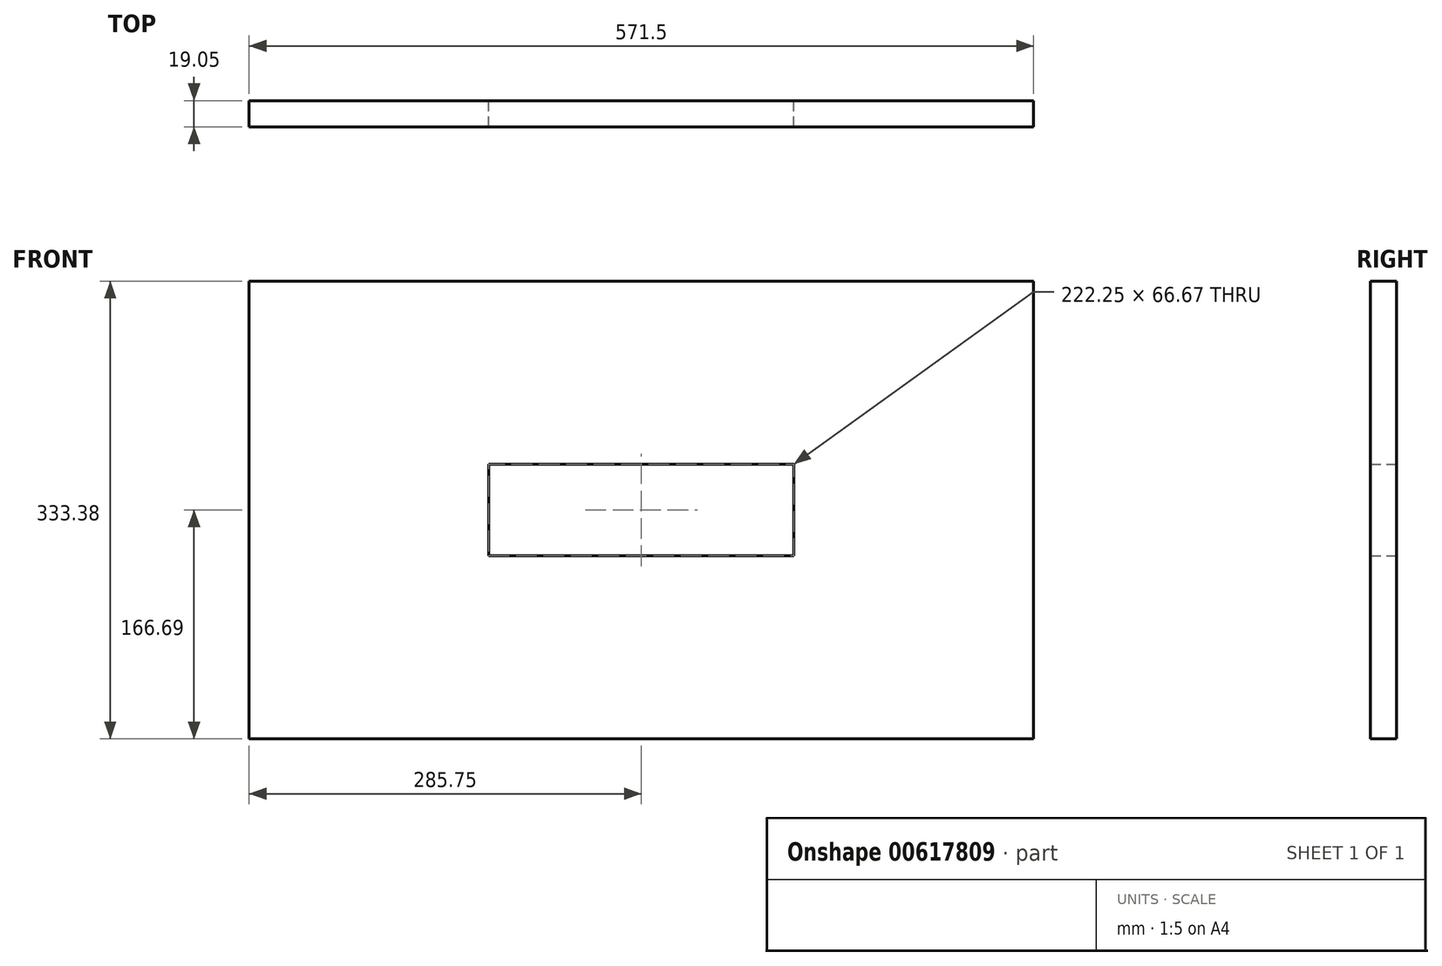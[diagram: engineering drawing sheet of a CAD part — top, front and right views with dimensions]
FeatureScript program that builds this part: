
annotation { "Feature Type Name" : "Feature", "Feature Type Description" : "" }
export const myFeature = defineFeature(function(context is Context, id is Id, definition is map)
    precondition{}
    {
        {
            var Q0;
            Q0=qCreatedBy(makeId("Front.planeOp"),FACE);
            var sketch = newSketch(context, id + "F0", { "sketchPlane" : qUnion([Q0])});
            skLineSegment(sketch, "E0.bottom", {"start": v(-285.75, 166.69) * mm, "end": v(285.75, 166.69) * mm});
            skLineSegment(sketch, "E0.top", {"start": v(-285.75, -166.69) * mm, "end": v(285.75, -166.69) * mm});
            skLineSegment(sketch, "E0.left", {"start": v(-285.75, 166.69) * mm, "end": v(-285.75, -166.69) * mm});
            skLineSegment(sketch, "E0.right", {"start": v(285.75, 166.69) * mm, "end": v(285.75, -166.69) * mm});
            skPoint(sketch, "E0.middle", {"position": v(0, 0) * mm});
            skLineSegment(sketch, "E1.bottom", {"start": v(111.13, 33.34) * mm, "end": v(-111.13, 33.34) * mm});
            skLineSegment(sketch, "E1.top", {"start": v(111.13, -33.34) * mm, "end": v(-111.13, -33.34) * mm});
            skLineSegment(sketch, "E1.left", {"start": v(111.13, 33.34) * mm, "end": v(111.13, -33.34) * mm});
            skLineSegment(sketch, "E1.right", {"start": v(-111.13, 33.34) * mm, "end": v(-111.13, -33.34) * mm});
            skSolve(sketch);
        }
        {
            var Q0;
            Q0=makeQuery(id+"F0.imprint","IMPRINT",FACE,{"disambiguationData":[TD([[makeQuery(id+"F0.imprint","IMPRINT",EDGE,{"derivedFrom":sQuery(id+"F0.wireOp",EDGE,"E0.bottom")}),-1.0]])]});
            extrude(context, id + "F1", {"entities" : qUnion([Q0]), "depth" : 19.05 * mm, "offsetDistance" : 25.4 * mm});
        }
    });
